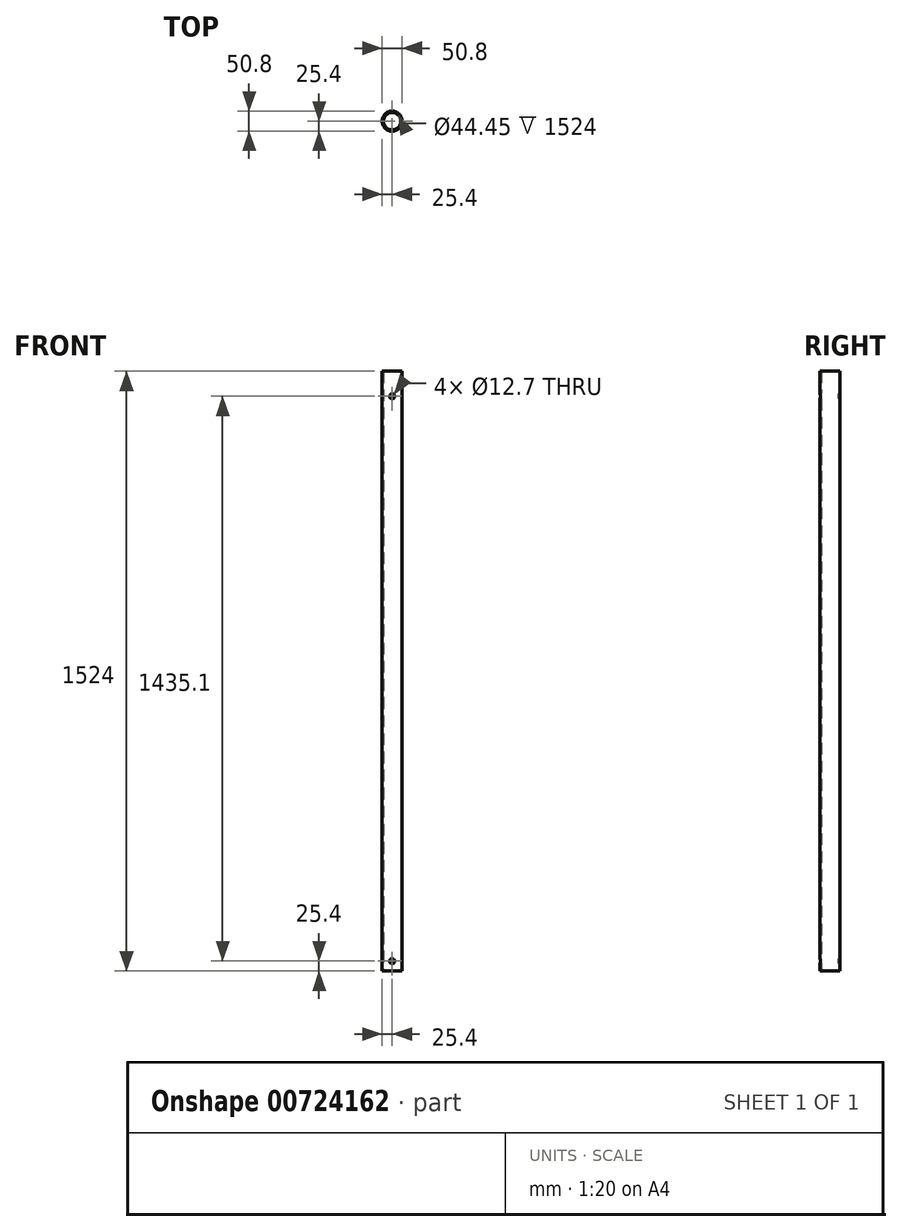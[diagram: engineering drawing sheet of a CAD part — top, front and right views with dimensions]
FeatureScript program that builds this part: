
annotation { "Feature Type Name" : "Feature", "Feature Type Description" : "" }
export const myFeature = defineFeature(function(context is Context, id is Id, definition is map)
    precondition{}
    {
        {
            var Q0;
            Q0=qCreatedBy(makeId("Top.planeOp"),FACE);
            var sketch = newSketch(context, id + "F0", { "sketchPlane" : qUnion([Q0])});
            skCircle(sketch, "E0", {"center": v(0, 0) * mm, "radius": 25.4 * mm});
            skCircle(sketch, "E1", {"center": v(0, 0) * mm, "radius": 22.23 * mm});
            skSolve(sketch);
        }
        {
            var Q0;
            Q0=makeQuery(id+"F0.imprint","IMPRINT",FACE,{"disambiguationData":[TD([[makeQuery(id+"F0.imprint","IMPRINT",EDGE,{"derivedFrom":sQuery(id+"F0.wireOp",EDGE,"E0")}),1.0]])]});
            extrude(context, id + "F1", {"entities" : qUnion([Q0]), "depth" : 1524 * mm, "offsetDistance" : 25.4 * mm});
        }
        {
            var Q0;
            Q0=qCreatedBy(makeId("Front.planeOp"),FACE);
            var sketch = newSketch(context, id + "F2", { "sketchPlane" : qUnion([Q0])});
            skLineSegment(sketch, "E2", {"start": v(0, 0) * mm, "end": v(0, 25.4) * mm, "construction": true});
            skLineSegment(sketch, "E3", {"start": v(0, 25.4) * mm, "end": v(0, 1460.5) * mm, "construction": true});
            skCircle(sketch, "E4", {"center": v(0, 1460.5) * mm, "radius": 6.35 * mm});
            skCircle(sketch, "E5", {"center": v(0, 25.4) * mm, "radius": 6.35 * mm});
            skSolve(sketch);
        }
        {
            var Q0;
            Q0=qSketchRegion(id+"F2",true);
            extrude(context, id + "F3", {"entities" : qUnion([Q0]), "operationType" : NewBodyOperationType.REMOVE, "oppositeDirection" : true, "depth" : 50.8 * mm, "offsetDistance" : 25.4 * mm, "symmetric" : true});
        }
    });
